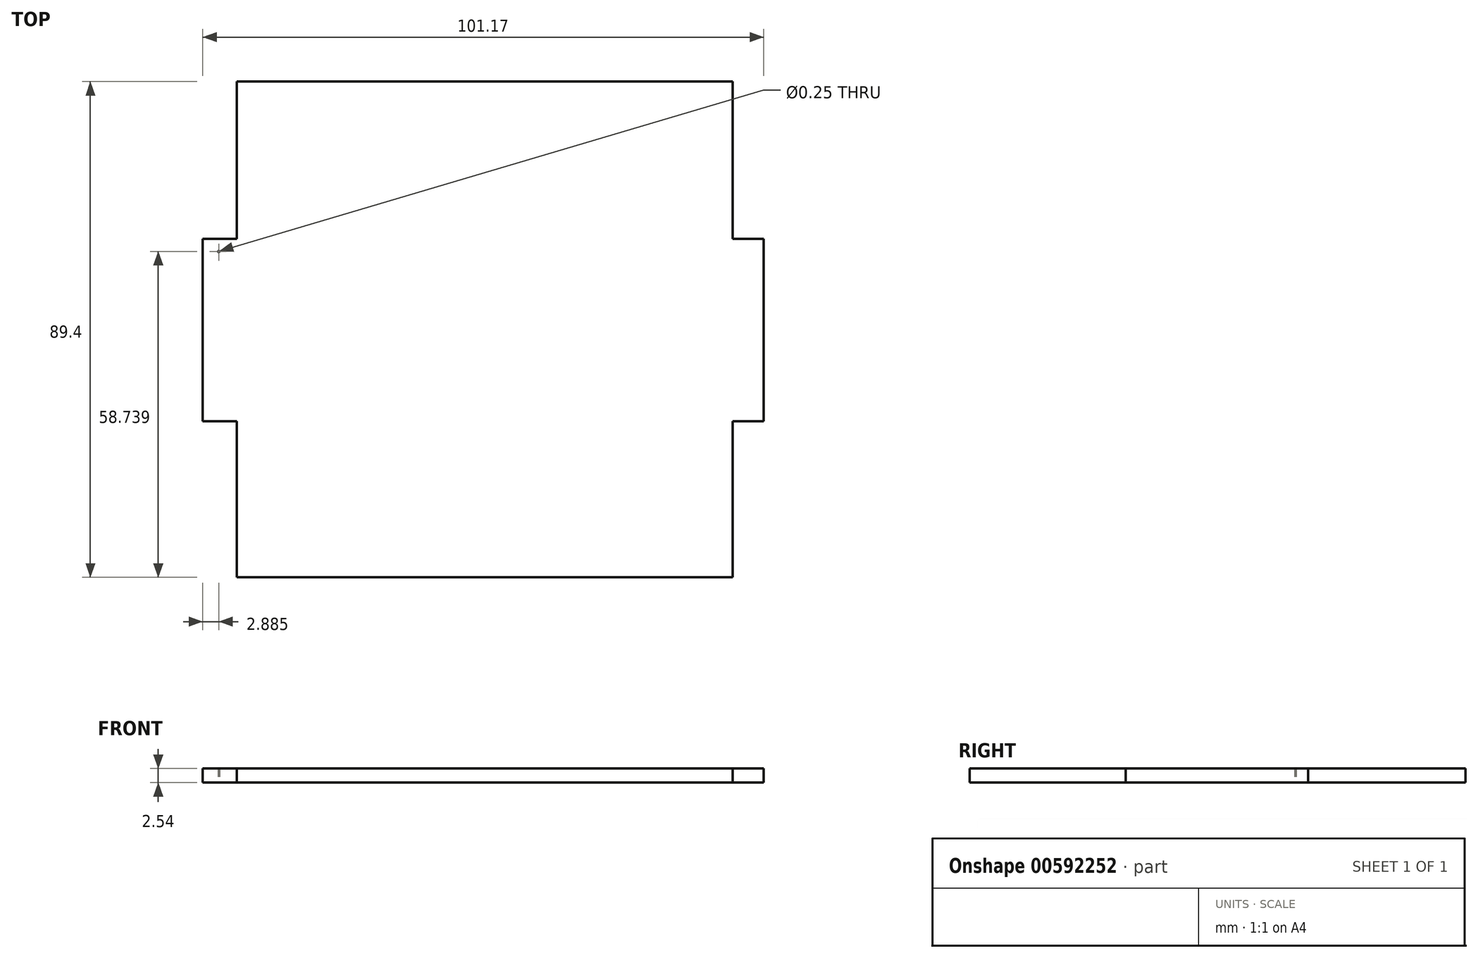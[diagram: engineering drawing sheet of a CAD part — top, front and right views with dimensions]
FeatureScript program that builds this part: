
annotation { "Feature Type Name" : "Feature", "Feature Type Description" : "" }
export const myFeature = defineFeature(function(context is Context, id is Id, definition is map)
    precondition{}
    {
        {
            var Q0;
            Q0=qCreatedBy(makeId("Top.planeOp"),FACE);
            var sketch = newSketch(context, id + "F0", { "sketchPlane" : qUnion([Q0])});
            skLineSegment(sketch, "E0.bottom", {"start": v(-44.7, 44.7) * mm, "end": v(44.7, 44.7) * mm});
            skLineSegment(sketch, "E0.top", {"start": v(-44.7, -44.7) * mm, "end": v(44.7, -44.7) * mm});
            skLineSegment(sketch, "E0.left", {"start": v(-44.7, 44.7) * mm, "end": v(-44.7, -44.7) * mm});
            skLineSegment(sketch, "E0.right", {"start": v(44.7, 44.7) * mm, "end": v(44.7, -44.7) * mm});
            skPoint(sketch, "E0.middle", {"position": v(0, 0) * mm});
            skLineSegment(sketch, "E1.bottom", {"start": v(-44.7, 16.35) * mm, "end": v(-50.88, 16.35) * mm});
            skLineSegment(sketch, "E1.top", {"start": v(-44.7, -16.55) * mm, "end": v(-50.88, -16.55) * mm});
            skLineSegment(sketch, "E1.left", {"start": v(-44.7, 16.35) * mm, "end": v(-44.7, -16.55) * mm});
            skLineSegment(sketch, "E1.right", {"start": v(-50.88, 16.35) * mm, "end": v(-50.88, -16.55) * mm});
            skLineSegment(sketch, "E2.bottom", {"start": v(44.7, 16.35) * mm, "end": v(50.3, 16.35) * mm});
            skLineSegment(sketch, "E2.top", {"start": v(44.7, -16.55) * mm, "end": v(50.3, -16.55) * mm});
            skLineSegment(sketch, "E2.left", {"start": v(44.7, 16.35) * mm, "end": v(44.7, -16.55) * mm});
            skLineSegment(sketch, "E2.right", {"start": v(50.3, 16.35) * mm, "end": v(50.3, -16.55) * mm});
            skSolve(sketch);
        }
        {
            var Q0;
            Q0 = qSketchRegion(id + "F0", true);
            extrude(context, id + "F1", {"entities" : qUnion([Q0]), "depth" : 2.54 * mm, "offsetDistance" : 25.4 * mm});
        }
        {
            var Q0;
            Q0=qCreatedBy(makeId("Top.planeOp"),FACE);
            var sketch = newSketch(context, id + "F2", { "sketchPlane" : qUnion([Q0])});
            skPoint(sketch, "E3", {"position": v(-48, 14.04) * mm});
            skSolve(sketch);
        }
        {
            var Q0;
            Q0=sQuery(id+"F2.wireOp",VERTEX,"E3");
            var Q1;
            Q1=makeQuery(id+"F1.opExtrude","SWEPT_BODY",BODY,{"disambiguationData":[OSD([sQuery(id+"F0.wireOp",EDGE,"E0.bottom"),sQuery(id+"F0.wireOp",EDGE,"E0.top"),sQuery(id+"F0.wireOp",EDGE,"E0.left"),sQuery(id+"F0.wireOp",EDGE,"E0.right"),sQuery(id+"F0.wireOp",EDGE,"E1.bottom"),sQuery(id+"F0.wireOp",EDGE,"E1.top"),sQuery(id+"F0.wireOp",EDGE,"E1.right"),sQuery(id+"F0.wireOp",EDGE,"E2.bottom"),sQuery(id+"F0.wireOp",EDGE,"E2.top"),sQuery(id+"F0.wireOp",EDGE,"E2.right")])]});
            hole(context, id + "F3", {"style" : HoleStyle.SIMPLE, "endStyle" : HoleEndStyle.THROUGH, "oppositeDirection" : true, "holeDiameter" : 0.25 * mm, "majorDiameter" : 6.35 * mm, "isTappedThrough" : true, "tappedDepth" : 12.7 * mm, "tapClearance" : 3, "locations" : qUnion([Q0]), "scope" : qUnion([Q1])});
        }
    });
